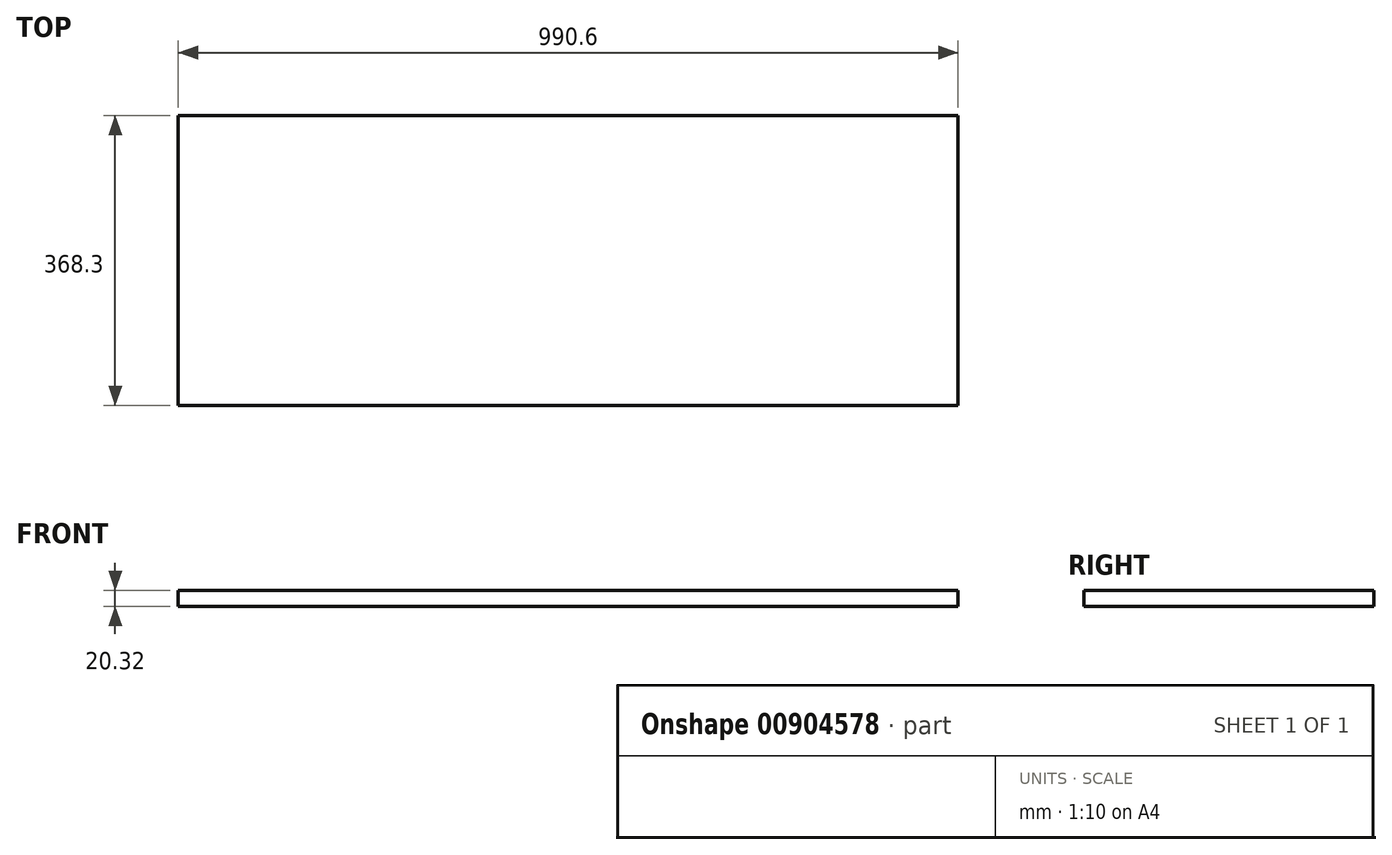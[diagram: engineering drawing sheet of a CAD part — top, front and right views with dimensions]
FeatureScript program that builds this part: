
annotation { "Feature Type Name" : "Feature", "Feature Type Description" : "" }
export const myFeature = defineFeature(function(context is Context, id is Id, definition is map)
    precondition{}
    {
        {
            var Q0;
            Q0=qCreatedBy(makeId("Top.planeOp"),FACE);
            var sketch = newSketch(context, id + "F0", { "sketchPlane" : qUnion([Q0])});
            skLineSegment(sketch, "E0.bottom", {"start": v(495.3, 184.15) * mm, "end": v(-495.3, 184.15) * mm});
            skLineSegment(sketch, "E0.top", {"start": v(495.3, -184.15) * mm, "end": v(-495.3, -184.15) * mm});
            skLineSegment(sketch, "E0.left", {"start": v(495.3, 184.15) * mm, "end": v(495.3, -184.15) * mm});
            skLineSegment(sketch, "E0.right", {"start": v(-495.3, 184.15) * mm, "end": v(-495.3, -184.15) * mm});
            skPoint(sketch, "E0.middle", {"position": v(0, 0) * mm});
            skSolve(sketch);
        }
        {
            var Q0;
            Q0 = qSketchRegion(id + "F0", true);
            extrude(context, id + "F1", {"entities" : qUnion([Q0]), "depth" : 20.32 * mm, "offsetDistance" : 25.4 * mm});
        }
    });
